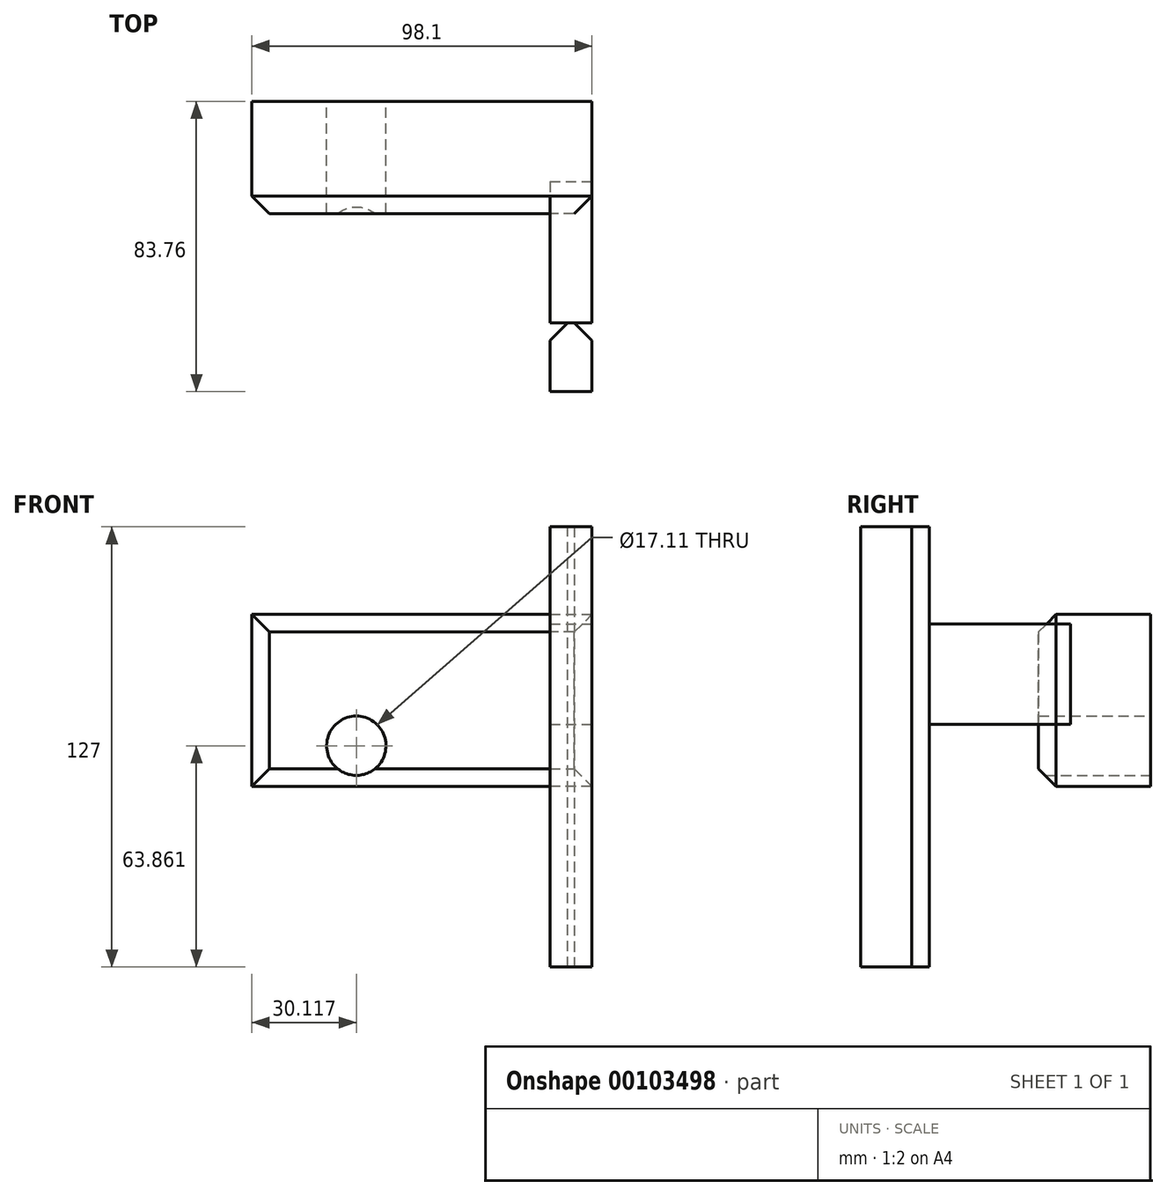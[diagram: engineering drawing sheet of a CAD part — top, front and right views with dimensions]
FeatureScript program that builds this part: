
annotation { "Feature Type Name" : "Feature", "Feature Type Description" : "" }
export const myFeature = defineFeature(function(context is Context, id is Id, definition is map)
    precondition{}
    {
        {
            var Q0;
            Q0=qCreatedBy(makeId("Top.planeOp"),FACE);
            var sketch = newSketch(context, id + "F0", { "sketchPlane" : qUnion([Q0])});
            skLineSegment(sketch, "E0.bottom", {"start": v(39.29, -31.54) * mm, "end": v(51.41, -31.54) * mm});
            skLineSegment(sketch, "E0.top", {"start": v(39.29, -51.4) * mm, "end": v(51.41, -51.4) * mm});
            skLineSegment(sketch, "E0.left", {"start": v(39.29, -31.54) * mm, "end": v(39.29, -51.4) * mm});
            skLineSegment(sketch, "E0.right", {"start": v(51.41, -31.54) * mm, "end": v(51.41, -51.4) * mm});
            skLineSegment(sketch, "E1.bottom", {"start": v(-14.76, 47.98) * mm, "end": v(-21.14, 47.98) * mm});
            skLineSegment(sketch, "E1.top", {"start": v(-14.76, 51.84) * mm, "end": v(-21.14, 51.84) * mm});
            skLineSegment(sketch, "E1.left", {"start": v(-14.76, 47.98) * mm, "end": v(-14.76, 51.84) * mm});
            skLineSegment(sketch, "E1.right", {"start": v(-21.14, 47.98) * mm, "end": v(-21.14, 51.84) * mm});
            skSolve(sketch);
        }
        {
            var Q0;
            Q0 = qBodyType(qCreatedBy(id + "F0" ,EDGE), BodyType.WIRE);
            var sketch = newSketch(context, id + "F1", { "sketchPlane" : qUnion([Q0])});
            skSolve(sketch);
        }
        {
            var Q0;
            Q0 = qSketchRegion(id + "F1", true);
            var Q1;
            Q1=makeQuery(id+"F0.imprint","IMPRINT",FACE,{"disambiguationData":[TD([[makeQuery(id+"F0.imprint","IMPRINT",EDGE,{"derivedFrom":sQuery(id+"F0.wireOp",EDGE,"E0.bottom")}),-1.0]])]});
            extrude(context, id + "F2", {"entities" : qUnion([Q0, Q1]), "depth" : 127 * mm});
        }
        {
            var Q0;
            Q0=makeQuery(id+"F2.opExtrude","SWEPT_FACE",FACE,{"disambiguationData":[OSD([sQuery(id+"F0.wireOp",EDGE,"E0.right")])]});
            var sketch = newSketch(context, id + "F3", { "sketchPlane" : qUnion([Q0])});
            skLineSegment(sketch, "E2.bottom", {"start": v(0, 52.12) * mm, "end": v(32.36, 52.12) * mm});
            skLineSegment(sketch, "E2.top", {"start": v(0, 101.73) * mm, "end": v(32.36, 101.73) * mm});
            skLineSegment(sketch, "E2.left", {"start": v(0, 52.12) * mm, "end": v(0, 101.73) * mm});
            skLineSegment(sketch, "E2.right", {"start": v(32.36, 52.12) * mm, "end": v(32.36, 101.73) * mm});
            skSolve(sketch);
        }
        {
            var Q0;
            Q0 = qSketchRegion(id + "F3", true);
            extrude(context, id + "F4", {"entities" : qUnion([Q0]), "oppositeDirection" : true, "depth" : 98.1 * mm});
        }
        {
            var Q0;
            Q0=makeQuery(id+"F4.opExtrude","SWEPT_FACE",FACE,{"disambiguationData":[OSD([sQuery(id+"F3.wireOp",EDGE,"E2.left")])]});
            var Q1;
            Q1=makeQuery(id+"F4.opExtrude","SWEPT_EDGE",EDGE,{"disambiguationData":[OSD([sQuery(id+"F3.wireOp",EDGE,"E2.bottom"),sQuery(id+"F3.wireOp",EDGE,"E2.left")])]});
            var Q2;
            Q2=makeQuery(id+"F2.opExtrude","SWEPT_EDGE",EDGE,{"disambiguationData":[OSD([sQuery(id+"F0.wireOp",EDGE,"E0.bottom"),sQuery(id+"F0.wireOp",EDGE,"E0.left")])]});
            var Q3;
            Q3=makeQuery(id+"F2.opExtrude","SWEPT_EDGE",EDGE,{"disambiguationData":[OSD([sQuery(id+"F0.wireOp",EDGE,"E0.bottom"),sQuery(id+"F0.wireOp",EDGE,"E0.right")])]});
            chamfer(context, id + "F5", {"entities" : qUnion([Q0, Q1, Q2, Q3]), "width" : 5.08 * mm, "tangentPropagation" : true});
        }
        {
            var Q0;
            Q0=makeQuery(id+"F2.opExtrude","SWEPT_FACE",FACE,{"disambiguationData":[OSD([sQuery(id+"F0.wireOp",EDGE,"E0.bottom")])]});
            var sketch = newSketch(context, id + "F6", { "sketchPlane" : qUnion([Q0])});
            skLineSegment(sketch, "E3.bottom", {"start": v(-39.29, 98.98) * mm, "end": v(-51.41, 98.98) * mm});
            skLineSegment(sketch, "E3.top", {"start": v(-39.29, 70) * mm, "end": v(-51.41, 70) * mm});
            skLineSegment(sketch, "E3.left", {"start": v(-39.29, 98.98) * mm, "end": v(-39.29, 70) * mm});
            skLineSegment(sketch, "E3.right", {"start": v(-51.41, 98.98) * mm, "end": v(-51.41, 70) * mm});
            skSolve(sketch);
        }
        {
            var Q0;
            Q0 = qSketchRegion(id + "F6", true);
            extrude(context, id + "F7", {"entities" : qUnion([Q0]), "depth" : 40.72 * mm});
        }
        {
            var Q0;
            Q0=makeQuery(id+"F4.opExtrude","SWEPT_FACE",FACE,{"disambiguationData":[OSD([sQuery(id+"F3.wireOp",EDGE,"E2.right")])]});
            var sketch = newSketch(context, id + "F8", { "sketchPlane" : qUnion([Q0])});
            skCircle(sketch, "E4", {"center": v(16.57, 63.86) * mm, "radius": 8.56 * mm});
            skSolve(sketch);
        }
        {
            var Q0;
            Q0 = qSketchRegion(id + "F8", true);
            extrude(context, id + "F9", {"entities" : qUnion([Q0]), "operationType" : NewBodyOperationType.REMOVE, "oppositeDirection" : true, "depth" : 81.8 * mm});
        }
    });
